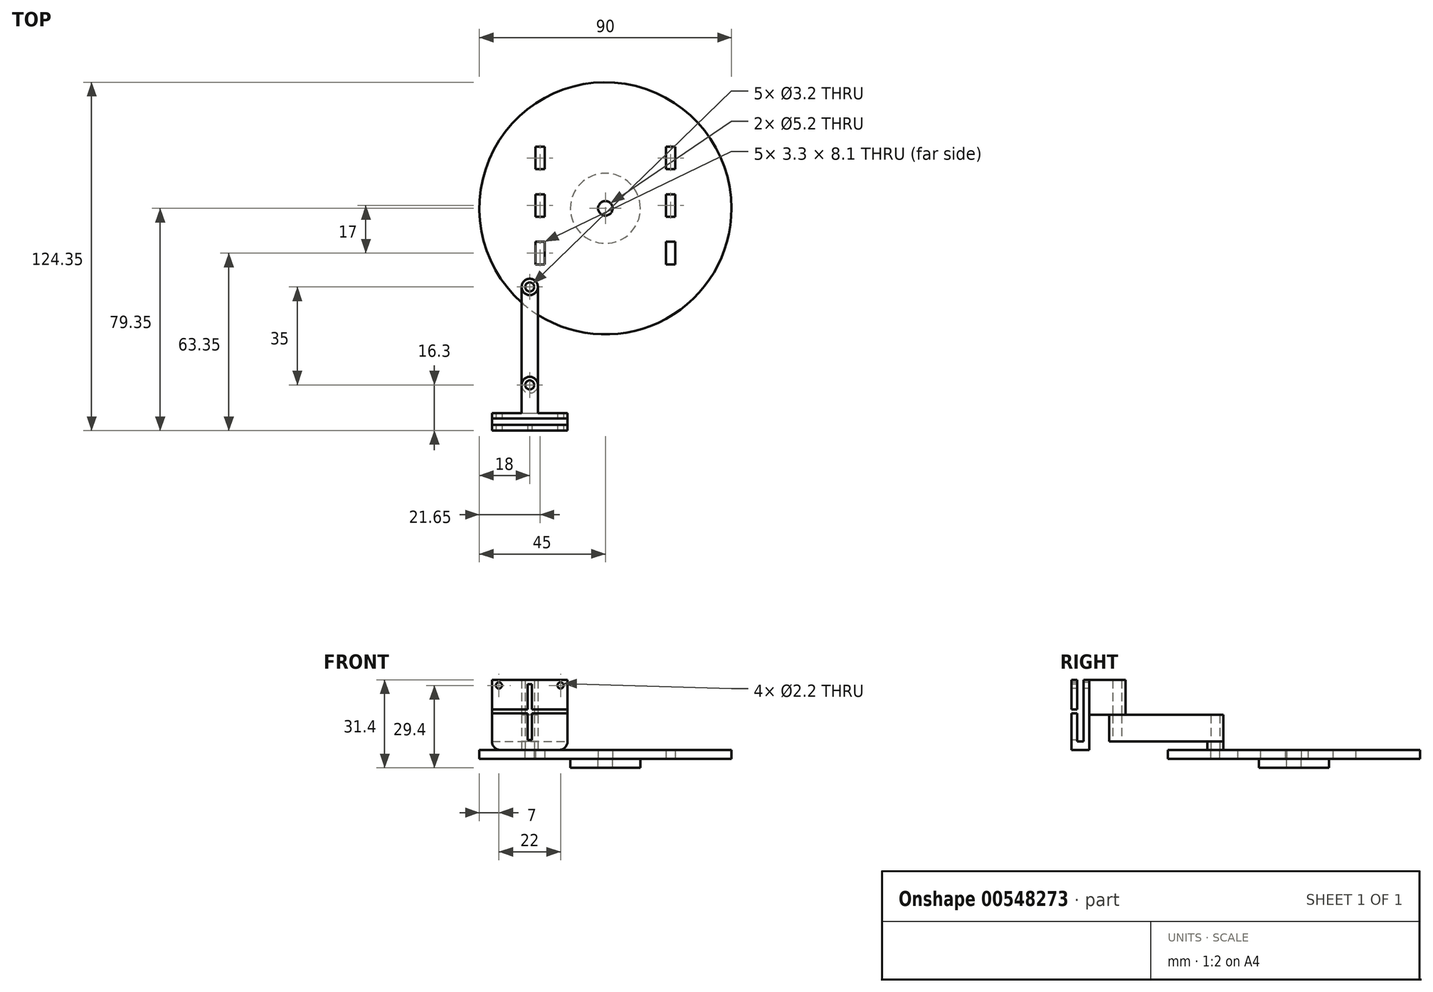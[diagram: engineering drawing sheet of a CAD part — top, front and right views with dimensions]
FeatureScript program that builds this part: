
annotation { "Feature Type Name" : "Feature", "Feature Type Description" : "" }
export const myFeature = defineFeature(function(context is Context, id is Id, definition is map)
    precondition{}
    {
        {
            var Q0;
            Q0=qCreatedBy(makeId("Top.planeOp"),FACE);
            var sketch = newSketch(context, id + "F0", { "sketchPlane" : qUnion([Q0])});
            skCircle(sketch, "E0", {"center": v(0, 0) * mm, "radius": 35.36 * mm});
            skLineSegment(sketch, "E1.bottom", {"start": v(25, 25) * mm, "end": v(-25, 25) * mm});
            skLineSegment(sketch, "E1.top", {"start": v(25, -25) * mm, "end": v(-25, -25) * mm});
            skLineSegment(sketch, "E1.left", {"start": v(25, 25) * mm, "end": v(25, -25) * mm});
            skLineSegment(sketch, "E1.right", {"start": v(-25, 25) * mm, "end": v(-25, -25) * mm});
            skLineSegment(sketch, "E2.bottom", {"start": v(-25, 22.05) * mm, "end": v(-21.7, 22.05) * mm});
            skLineSegment(sketch, "E2.top", {"start": v(-25, 13.95) * mm, "end": v(-21.7, 13.95) * mm});
            skLineSegment(sketch, "E2.left", {"start": v(-25, 22.05) * mm, "end": v(-25, 13.95) * mm});
            skLineSegment(sketch, "E2.right", {"start": v(-21.7, 22.05) * mm, "end": v(-21.7, 13.95) * mm});
            skLineSegment(sketch, "E3.bottom", {"start": v(-25, 5.05) * mm, "end": v(-21.7, 5.05) * mm});
            skLineSegment(sketch, "E3.top", {"start": v(-25, -3.05) * mm, "end": v(-21.7, -3.05) * mm});
            skLineSegment(sketch, "E3.left", {"start": v(-25, 5.05) * mm, "end": v(-25, -3.05) * mm});
            skLineSegment(sketch, "E3.right", {"start": v(-21.7, 5.05) * mm, "end": v(-21.7, -3.05) * mm});
            skLineSegment(sketch, "E4.bottom", {"start": v(-25, -11.95) * mm, "end": v(-21.7, -11.95) * mm});
            skLineSegment(sketch, "E4.top", {"start": v(-25, -20.05) * mm, "end": v(-21.7, -20.05) * mm});
            skLineSegment(sketch, "E4.left", {"start": v(-25, -11.95) * mm, "end": v(-25, -20.05) * mm});
            skLineSegment(sketch, "E4.right", {"start": v(-21.7, -11.95) * mm, "end": v(-21.7, -20.05) * mm});
            skLineSegment(sketch, "E5.bottom", {"start": v(25, 22.05) * mm, "end": v(21.7, 22.05) * mm});
            skLineSegment(sketch, "E5.top", {"start": v(25, 13.95) * mm, "end": v(21.7, 13.95) * mm});
            skLineSegment(sketch, "E5.left", {"start": v(25, 22.05) * mm, "end": v(25, 13.95) * mm});
            skLineSegment(sketch, "E5.right", {"start": v(21.7, 22.05) * mm, "end": v(21.7, 13.95) * mm});
            skLineSegment(sketch, "E6.bottom", {"start": v(25, 5.05) * mm, "end": v(21.7, 5.05) * mm});
            skLineSegment(sketch, "E6.top", {"start": v(25, -3.05) * mm, "end": v(21.7, -3.05) * mm});
            skLineSegment(sketch, "E6.left", {"start": v(25, 5.05) * mm, "end": v(25, -3.05) * mm});
            skLineSegment(sketch, "E6.right", {"start": v(21.7, 5.05) * mm, "end": v(21.7, -3.05) * mm});
            skLineSegment(sketch, "E7.bottom", {"start": v(25, -11.95) * mm, "end": v(21.6, -11.95) * mm});
            skLineSegment(sketch, "E7.top", {"start": v(25, -20.05) * mm, "end": v(21.6, -20.05) * mm});
            skLineSegment(sketch, "E7.left", {"start": v(25, -11.95) * mm, "end": v(25, -20.05) * mm});
            skLineSegment(sketch, "E7.right", {"start": v(21.6, -11.95) * mm, "end": v(21.6, -20.05) * mm});
            skCircle(sketch, "E8", {"center": v(0, 0) * mm, "radius": 2.6 * mm});
            skSolve(sketch);
        }
        {
            var Q0;
            Q0=qSketchRegion(id+"F0",true);
            extrude(context, id + "F1", {"entities" : qUnion([Q0]), "depth" : 3.2 * mm, "offsetDistance" : 25 * mm});
        }
        {
            var Q0;
            Q0=qCreatedBy(makeId("Top.planeOp"),FACE);
            var sketch = newSketch(context, id + "F2", { "sketchPlane" : qUnion([Q0])});
            skCircle(sketch, "E9", {"center": v(0, 0) * mm, "radius": 45 * mm});
            skCircle(sketch, "E10", {"center": v(0, 0) * mm, "radius": 35.36 * mm});
            skSolve(sketch);
        }
        {
            var Q0;
            Q0=qSketchRegion(id+"F2",true);
            var Q1;
            Q1=makeQuery(id+"F1.opExtrude","CAP_FACE",FACE,{"disambiguationData":[OSD([sQuery(id+"F0.wireOp",EDGE,"E0"),sQuery(id+"F0.wireOp",EDGE,"E2.bottom"),sQuery(id+"F0.wireOp",EDGE,"E2.top"),sQuery(id+"F0.wireOp",EDGE,"E2.left"),sQuery(id+"F0.wireOp",EDGE,"E2.right"),sQuery(id+"F0.wireOp",EDGE,"E3.bottom"),sQuery(id+"F0.wireOp",EDGE,"E3.top"),sQuery(id+"F0.wireOp",EDGE,"E3.left"),sQuery(id+"F0.wireOp",EDGE,"E3.right"),sQuery(id+"F0.wireOp",EDGE,"E4.bottom"),sQuery(id+"F0.wireOp",EDGE,"E4.top"),sQuery(id+"F0.wireOp",EDGE,"E4.left"),sQuery(id+"F0.wireOp",EDGE,"E4.right"),sQuery(id+"F0.wireOp",EDGE,"E5.bottom"),sQuery(id+"F0.wireOp",EDGE,"E5.top"),sQuery(id+"F0.wireOp",EDGE,"E5.left"),sQuery(id+"F0.wireOp",EDGE,"E5.right"),sQuery(id+"F0.wireOp",EDGE,"E6.bottom"),sQuery(id+"F0.wireOp",EDGE,"E6.top"),sQuery(id+"F0.wireOp",EDGE,"E6.left"),sQuery(id+"F0.wireOp",EDGE,"E6.right"),sQuery(id+"F0.wireOp",EDGE,"E7.bottom"),sQuery(id+"F0.wireOp",EDGE,"E7.top"),sQuery(id+"F0.wireOp",EDGE,"E7.left"),sQuery(id+"F0.wireOp",EDGE,"E7.right"),sQuery(id+"F0.wireOp",EDGE,"E8")])],"isStart":false});
            extrude(context, id + "F3", {"entities" : qUnion([Q0]), "operationType" : NewBodyOperationType.ADD, "endBound" : BoundingType.UP_TO_SURFACE, "depth" : 25 * mm, "endBoundEntityFace" : qUnion([Q1]), "offsetDistance" : 25 * mm});
        }
        {
            var Q0;
            {var subQ0=sQuery(id+"F0.wireOp",EDGE,"E8");var subQ1=sQuery(id+"F0.wireOp",EDGE,"E7.right");var subQ2=sQuery(id+"F0.wireOp",EDGE,"E7.left");var subQ3=sQuery(id+"F0.wireOp",EDGE,"E7.top");var subQ4=sQuery(id+"F0.wireOp",EDGE,"E7.bottom");var subQ5=sQuery(id+"F0.wireOp",EDGE,"E6.right");var subQ6=sQuery(id+"F0.wireOp",EDGE,"E6.left");var subQ7=sQuery(id+"F0.wireOp",EDGE,"E6.top");var subQ8=sQuery(id+"F0.wireOp",EDGE,"E6.bottom");var subQ9=sQuery(id+"F0.wireOp",EDGE,"E5.right");var subQ10=sQuery(id+"F0.wireOp",EDGE,"E5.left");var subQ11=sQuery(id+"F0.wireOp",EDGE,"E5.top");var subQ12=sQuery(id+"F0.wireOp",EDGE,"E5.bottom");var subQ13=sQuery(id+"F0.wireOp",EDGE,"E4.right");var subQ14=sQuery(id+"F0.wireOp",EDGE,"E4.left");var subQ15=sQuery(id+"F0.wireOp",EDGE,"E4.top");var subQ16=sQuery(id+"F0.wireOp",EDGE,"E4.bottom");var subQ17=sQuery(id+"F0.wireOp",EDGE,"E3.right");var subQ18=sQuery(id+"F0.wireOp",EDGE,"E3.left");var subQ19=sQuery(id+"F0.wireOp",EDGE,"E3.top");var subQ20=sQuery(id+"F0.wireOp",EDGE,"E3.bottom");var subQ21=sQuery(id+"F0.wireOp",EDGE,"E2.right");var subQ22=sQuery(id+"F0.wireOp",EDGE,"E2.left");var subQ23=sQuery(id+"F0.wireOp",EDGE,"E2.top");var subQ24=sQuery(id+"F0.wireOp",EDGE,"E2.bottom");var subQ25=sQuery(id+"F0.wireOp",EDGE,"E0");Q0=makeQuery(id+"F3.boolean.opBoolean","MERGE",FACE,{"derivedFrom":[makeQuery(id+"F1.opExtrude","CAP_FACE",FACE,{"disambiguationData":[OSD([subQ25,subQ24,subQ23,subQ22,subQ21,subQ20,subQ19,subQ18,subQ17,subQ16,subQ15,subQ14,subQ13,subQ12,subQ11,subQ10,subQ9,subQ8,subQ7,subQ6,subQ5,subQ4,subQ3,subQ2,subQ1,subQ0])],"isStart":false}),makeQuery(id+"F3.opExtrude","CAP_FACE",FACE,{"disambiguationData":[OSD([subQ25,subQ24,subQ23,subQ22,subQ21,subQ20,subQ19,subQ18,subQ17,subQ16,subQ15,subQ14,subQ13,subQ12,subQ11,subQ10,subQ9,subQ8,subQ7,subQ6,subQ5,subQ4,subQ3,subQ2,subQ1,subQ0])],"isStart":false})]});}
            var sketch = newSketch(context, id + "F4", { "sketchPlane" : qUnion([Q0])});
            skCircle(sketch, "E11", {"center": v(-27, -28.05) * mm, "radius": 1.6 * mm});
            skCircle(sketch, "E12", {"center": v(-27, -28.05) * mm, "radius": 2.9 * mm});
            skSolve(sketch);
        }
        {
            var Q0;
            Q0=makeQuery(id+"F4.imprint","IMPRINT",FACE,{"disambiguationData":[TD([[makeQuery(id+"F4.imprint","IMPRINT",EDGE,{"derivedFrom":sQuery(id+"F4.wireOp",EDGE,"E11")}),1.0]])]});
            var Q1;
            Q1=sQuery(id+"F4.wireOp",EDGE,"E11");
            var Q2;
            Q2=makeQuery(id+"F3.boolean.opBoolean","MERGE",FACE,{"derivedFrom":[makeQuery(id+"F1.opExtrude","CAP_FACE",FACE,{"disambiguationData":[OSD([sQuery(id+"F0.wireOp",EDGE,"E0"),sQuery(id+"F0.wireOp",EDGE,"E2.bottom"),sQuery(id+"F0.wireOp",EDGE,"E2.top"),sQuery(id+"F0.wireOp",EDGE,"E2.left"),sQuery(id+"F0.wireOp",EDGE,"E2.right"),sQuery(id+"F0.wireOp",EDGE,"E3.bottom"),sQuery(id+"F0.wireOp",EDGE,"E3.top"),sQuery(id+"F0.wireOp",EDGE,"E3.left"),sQuery(id+"F0.wireOp",EDGE,"E3.right"),sQuery(id+"F0.wireOp",EDGE,"E4.bottom"),sQuery(id+"F0.wireOp",EDGE,"E4.top"),sQuery(id+"F0.wireOp",EDGE,"E4.left"),sQuery(id+"F0.wireOp",EDGE,"E4.right"),sQuery(id+"F0.wireOp",EDGE,"E5.bottom"),sQuery(id+"F0.wireOp",EDGE,"E5.top"),sQuery(id+"F0.wireOp",EDGE,"E5.left"),sQuery(id+"F0.wireOp",EDGE,"E5.right"),sQuery(id+"F0.wireOp",EDGE,"E6.bottom"),sQuery(id+"F0.wireOp",EDGE,"E6.top"),sQuery(id+"F0.wireOp",EDGE,"E6.left"),sQuery(id+"F0.wireOp",EDGE,"E6.right"),sQuery(id+"F0.wireOp",EDGE,"E7.bottom"),sQuery(id+"F0.wireOp",EDGE,"E7.top"),sQuery(id+"F0.wireOp",EDGE,"E7.left"),sQuery(id+"F0.wireOp",EDGE,"E7.right"),sQuery(id+"F0.wireOp",EDGE,"E8")])],"isStart":true}),makeQuery(id+"F3.opExtrude","CAP_FACE",FACE,{"disambiguationData":[OSD([sQuery(id+"F2.wireOp",EDGE,"E9"),sQuery(id+"F2.wireOp",EDGE,"E10")])],"isStart":true})]});
            extrude(context, id + "F5", {"entities" : qUnion([Q0]), "operationType" : NewBodyOperationType.REMOVE, "surfaceEntities" : qUnion([Q1]), "endBound" : BoundingType.UP_TO_SURFACE, "oppositeDirection" : true, "depth" : 25 * mm, "endBoundEntityFace" : qUnion([Q2]), "offsetDistance" : 25 * mm});
        }
        {
            var Q0;
            Q0=makeQuery(id+"F4.imprint","IMPRINT",FACE,{"disambiguationData":[TD([[makeQuery(id+"F4.imprint","IMPRINT",EDGE,{"derivedFrom":sQuery(id+"F4.wireOp",EDGE,"E11")}),-1.0]])]});
            extrude(context, id + "F6", {"entities" : qUnion([Q0]), "depth" : 2.5 * mm, "offsetDistance" : 25 * mm});
        }
        {
            var Q0;
            Q0=makeQuery(id+"F4.imprint","IMPRINT",FACE,{"disambiguationData":[TD([[makeQuery(id+"F4.imprint","IMPRINT",EDGE,{"derivedFrom":sQuery(id+"F4.wireOp",EDGE,"IzYP4Wh4-Jip2-t4EX-ThSt-IXmmCnc5qann")}),-1.0]])]});
            var Q1;
            {var subQ0=sQuery(id+"F4.wireOp",EDGE,"7peC47Pw-5aqN-fUO1-vEJ7-lQEhbhiZa9DA");var subQ1=sQuery(id+"F4.wireOp",EDGE,"wxSrbtV1-SH39-PG1R-bbc8-Dl0xVSDKGow7");var subQ2=makeQuery(id+"F4.imprint","INTERSECT",VERTEX,{"derivedFrom":[subQ1,subQ0]});Q1=makeQuery(id+"F4.imprint","IMPRINT",FACE,{"disambiguationData":[TD([[makeQuery(id+"F4.imprint","IMPRINT",EDGE,{"disambiguationData":[TD([[subQ2,1.0]])],"derivedFrom":subQ0}),-1.0]])]});}
            var Q2;
            Q2=makeQuery(id+"F4.imprint","IMPRINT",FACE,{"disambiguationData":[TD([[makeQuery(id+"F4.imprint","IMPRINT",EDGE,{"derivedFrom":sQuery(id+"F4.wireOp",EDGE,"E11")}),-1.0]])]});
            var Q3;
            {var subQ0=sQuery(id+"F4.wireOp",EDGE,"wxSrbtV1-SH39-PG1R-bbc8-Dl0xVSDKGow7");var subQ1=sQuery(id+"F4.wireOp",EDGE,"E12");var subQ2=makeQuery(id+"F4.imprint","INTERSECT",VERTEX,{"derivedFrom":[subQ1,subQ0]});Q3=makeQuery(id+"F4.imprint","IMPRINT",FACE,{"disambiguationData":[TD([[makeQuery(id+"F4.imprint","IMPRINT",EDGE,{"disambiguationData":[TD([[subQ2,-1.0]])],"derivedFrom":subQ1}),-1.0]])]});}
            var Q4;
            Q4=sQuery(id+"F4.wireOp",EDGE,"IzYP4Wh4-Jip2-t4EX-ThSt-IXmmCnc5qann");
            var Q5;
            Q5=sQuery(id+"F4.wireOp",EDGE,"7peC47Pw-5aqN-fUO1-vEJ7-lQEhbhiZa9DA");
            var Q6;
            Q6=sQuery(id+"F4.wireOp",EDGE,"9hU6XA7T-7hqy-5dnO-gkdG-iSiWrYzMhXLp");
            var Q7;
            Q7=sQuery(id+"F4.wireOp",EDGE,"wxSrbtV1-SH39-PG1R-bbc8-Dl0xVSDKGow7");
            var Q8;
            Q8=sQuery(id+"F4.wireOp",EDGE,"E11");
            var Q9;
            Q9=sQuery(id+"F4.wireOp",EDGE,"E12");
            extrude(context, id + "F7", {"entities" : qUnion([Q0, Q1, Q2, Q3]), "surfaceEntities" : qUnion([Q4, Q5, Q6, Q7, Q8, Q9]), "depth" : 12 * mm, "offsetDistance" : 25 * mm});
        }
        {
            var Q0;
            Q0=makeQuery(id+"F7.opExtrude","SWEPT_BODY",BODY,{"disambiguationData":[OSD([sQuery(id+"F4.wireOp",EDGE,"E11"),sQuery(id+"F4.wireOp",EDGE,"E12"),sQuery(id+"F4.wireOp",EDGE,"wxSrbtV1-SH39-PG1R-bbc8-Dl0xVSDKGow7"),sQuery(id+"F4.wireOp",EDGE,"9hU6XA7T-7hqy-5dnO-gkdG-iSiWrYzMhXLp"),sQuery(id+"F4.wireOp",EDGE,"7peC47Pw-5aqN-fUO1-vEJ7-lQEhbhiZa9DA"),sQuery(id+"F4.wireOp",EDGE,"IzYP4Wh4-Jip2-t4EX-ThSt-IXmmCnc5qann")])]});
            var Q1;
            Q1=makeQuery(id+"F6.opExtrude","SWEPT_BODY",BODY,{"disambiguationData":[OSD([sQuery(id+"F4.wireOp",EDGE,"E11"),sQuery(id+"F4.wireOp",EDGE,"E12")])]});
            deleteBodies(context, id + "F8", {"entities" : qUnion([Q0, Q1])});
        }
        {
            var Q0;
            Q0=makeQuery(id+"F4.imprint","IMPRINT",FACE,{"disambiguationData":[TD([[makeQuery(id+"F4.imprint","IMPRINT",EDGE,{"derivedFrom":sQuery(id+"F4.wireOp",EDGE,"E11")}),-1.0]])]});
            extrude(context, id + "F9", {"entities" : qUnion([Q0]), "depth" : 3 * mm, "offsetDistance" : 25 * mm});
        }
        {
            var Q0;
            Q0=makeQuery(id+"F9.opExtrude","CAP_FACE",FACE,{"disambiguationData":[OSD([sQuery(id+"F4.wireOp",EDGE,"E11"),sQuery(id+"F4.wireOp",EDGE,"E12")])],"isStart":false});
            var sketch = newSketch(context, id + "F10", { "sketchPlane" : qUnion([Q0])});
            skCircle(sketch, "E13", {"center": v(-27, -28.05) * mm, "radius": 1.6 * mm});
            skCircle(sketch, "E14", {"center": v(-27, -28.05) * mm, "radius": 2.9 * mm});
            skCircle(sketch, "E15", {"center": v(-27, -63.05) * mm, "radius": 1.6 * mm});
            skCircle(sketch, "E16", {"center": v(-27, -63.05) * mm, "radius": 2.9 * mm});
            skLineSegment(sketch, "E17", {"start": v(-29.9, -28.05) * mm, "end": v(-29.9, -63.05) * mm});
            skLineSegment(sketch, "E18", {"start": v(-24.1, -28.05) * mm, "end": v(-24.1, -63.05) * mm});
            skSolve(sketch);
        }
        {
            var Q0;
            Q0=qSketchRegion(id+"F10",true);
            extrude(context, id + "F11", {"entities" : qUnion([Q0]), "depth" : 9.5 * mm, "offsetDistance" : 25 * mm});
        }
        {
            var Q0;
            Q0=makeQuery(id+"F3.boolean.opBoolean","MERGE",FACE,{"derivedFrom":[makeQuery(id+"F1.opExtrude","CAP_FACE",FACE,{"disambiguationData":[OSD([sQuery(id+"F0.wireOp",EDGE,"E0"),sQuery(id+"F0.wireOp",EDGE,"E2.bottom"),sQuery(id+"F0.wireOp",EDGE,"E2.top"),sQuery(id+"F0.wireOp",EDGE,"E2.left"),sQuery(id+"F0.wireOp",EDGE,"E2.right"),sQuery(id+"F0.wireOp",EDGE,"E3.bottom"),sQuery(id+"F0.wireOp",EDGE,"E3.top"),sQuery(id+"F0.wireOp",EDGE,"E3.left"),sQuery(id+"F0.wireOp",EDGE,"E3.right"),sQuery(id+"F0.wireOp",EDGE,"E4.bottom"),sQuery(id+"F0.wireOp",EDGE,"E4.top"),sQuery(id+"F0.wireOp",EDGE,"E4.left"),sQuery(id+"F0.wireOp",EDGE,"E4.right"),sQuery(id+"F0.wireOp",EDGE,"E5.bottom"),sQuery(id+"F0.wireOp",EDGE,"E5.top"),sQuery(id+"F0.wireOp",EDGE,"E5.left"),sQuery(id+"F0.wireOp",EDGE,"E5.right"),sQuery(id+"F0.wireOp",EDGE,"E6.bottom"),sQuery(id+"F0.wireOp",EDGE,"E6.top"),sQuery(id+"F0.wireOp",EDGE,"E6.left"),sQuery(id+"F0.wireOp",EDGE,"E6.right"),sQuery(id+"F0.wireOp",EDGE,"E7.bottom"),sQuery(id+"F0.wireOp",EDGE,"E7.top"),sQuery(id+"F0.wireOp",EDGE,"E7.left"),sQuery(id+"F0.wireOp",EDGE,"E7.right"),sQuery(id+"F0.wireOp",EDGE,"E8")])],"isStart":true}),makeQuery(id+"F3.opExtrude","CAP_FACE",FACE,{"disambiguationData":[OSD([sQuery(id+"F2.wireOp",EDGE,"E9"),sQuery(id+"F2.wireOp",EDGE,"E10")])],"isStart":true})]});
            var sketch = newSketch(context, id + "F12", { "sketchPlane" : qUnion([Q0])});
            skCircle(sketch, "E19", {"center": v(0, 0) * mm, "radius": 12.5 * mm});
            skSolve(sketch);
        }
        {
            var Q0;
            Q0=makeQuery(id+"F12.imprint","IMPRINT",FACE,{"disambiguationData":[TD([[makeQuery(id+"F12.imprint","IMPRINT",EDGE,{"derivedFrom":sQuery(id+"F12.wireOp",EDGE,"E19")}),1.0]])]});
            extrude(context, id + "F13", {"entities" : qUnion([Q0]), "depth" : 3.2 * mm, "offsetDistance" : 25 * mm});
        }
        {
            var Q0;
            Q0=makeQuery(id+"F11.opExtrude","CAP_FACE",FACE,{"disambiguationData":[OSD([sQuery(id+"F10.wireOp",EDGE,"E13"),sQuery(id+"F10.wireOp",EDGE,"E14"),sQuery(id+"F10.wireOp",EDGE,"E15"),sQuery(id+"F10.wireOp",EDGE,"E16"),sQuery(id+"F10.wireOp",EDGE,"E17"),sQuery(id+"F10.wireOp",EDGE,"E18")])],"isStart":false});
            var sketch = newSketch(context, id + "F14", { "sketchPlane" : qUnion([Q0])});
            skCircle(sketch, "E20", {"center": v(-27, -63.05) * mm, "radius": 1.6 * mm});
            skCircle(sketch, "E21", {"center": v(-27, -63.05) * mm, "radius": 2.9 * mm});
            skLineSegment(sketch, "E22", {"start": v(-29.9, -63.05) * mm, "end": v(-29.9, -73.05) * mm});
            skLineSegment(sketch, "E23", {"start": v(-24.1, -63.05) * mm, "end": v(-24.1, -73.05) * mm});
            skLineSegment(sketch, "E24", {"start": v(-29.9, -73.05) * mm, "end": v(-24.1, -73.05) * mm});
            skSolve(sketch);
        }
        {
            var Q0;
            Q0=qSketchRegion(id+"F14",true);
            extrude(context, id + "F15", {"entities" : qUnion([Q0]), "depth" : 12.5 * mm, "offsetDistance" : 25 * mm});
        }
        {
            var Q0;
            Q0=makeQuery(id+"F15.opExtrude","CAP_FACE",FACE,{"disambiguationData":[OSD([sQuery(id+"F14.wireOp",EDGE,"E20"),sQuery(id+"F14.wireOp",EDGE,"E21"),sQuery(id+"F14.wireOp",EDGE,"E22"),sQuery(id+"F14.wireOp",EDGE,"E23"),sQuery(id+"F14.wireOp",EDGE,"E24")])],"isStart":false});
            var sketch = newSketch(context, id + "F16", { "sketchPlane" : qUnion([Q0])});
            skLineSegment(sketch, "E25", {"start": v(-40.5, -73.05) * mm, "end": v(-13.5, -73.05) * mm});
            skLineSegment(sketch, "E26", {"start": v(-40.5, -73.05) * mm, "end": v(-40.5, -79.35) * mm});
            skLineSegment(sketch, "E27", {"start": v(-13.5, -73.05) * mm, "end": v(-13.5, -79.35) * mm});
            skLineSegment(sketch, "E28", {"start": v(-40.5, -79.35) * mm, "end": v(-13.5, -79.35) * mm});
            skLineSegment(sketch, "E29", {"start": v(-40.5, -75.05) * mm, "end": v(-13.5, -75.05) * mm});
            skLineSegment(sketch, "E30", {"start": v(-40.5, -77.35) * mm, "end": v(-13.5, -77.35) * mm});
            skLineSegment(sketch, "E31", {"start": v(-27.75, -77.35) * mm, "end": v(-27.75, -79.35) * mm});
            skLineSegment(sketch, "E32", {"start": v(-26.25, -77.35) * mm, "end": v(-26.25, -79.35) * mm});
            skSolve(sketch);
        }
        {
            var Q0;
            Q0=qSketchRegion(id+"F16",true);
            extrude(context, id + "F17", {"entities" : qUnion([Q0]), "operationType" : NewBodyOperationType.ADD, "oppositeDirection" : true, "depth" : 25 * mm, "offsetDistance" : 25 * mm});
        }
        {
            var Q0;
            Q0=makeQuery(id+"F17.opExtrude","CAP_EDGE",EDGE,{"disambiguationData":[OSD([sQuery(id+"F16.wireOp",EDGE,"E26")])],"isStart":false});
            var Q1;
            Q1=makeQuery(id+"F17.opExtrude","CAP_EDGE",EDGE,{"disambiguationData":[OSD([sQuery(id+"F16.wireOp",EDGE,"E27")])],"isStart":false});
            fillet(context, id + "F18", {"entities" : qUnion([Q0, Q1]), "radius" : 3 * mm, "tangentPropagation" : true, "allowEdgeOverflow" : false});
        }
        {
            var Q0;
            {var subQ0=sQuery(id+"F16.wireOp",EDGE,"E29");Q0=makeQuery(id+"F16.imprint","IMPRINT",FACE,{"disambiguationData":[TD([[makeQuery(id+"F16.imprint","IMPRINT",EDGE,{"derivedFrom":subQ0}),-1.0]])]});}
            extrude(context, id + "F19", {"entities" : qUnion([Q0]), "operationType" : NewBodyOperationType.REMOVE, "oppositeDirection" : true, "depth" : 22 * mm, "offsetDistance" : 25 * mm});
        }
        {
            var Q0;
            {var subQ0=sQuery(id+"F16.wireOp",EDGE,"E28");Q0=makeQuery(id+"F16.imprint","IMPRINT",FACE,{"disambiguationData":[TD([[makeQuery(id+"F16.imprint","IMPRINT",EDGE,{"derivedFrom":subQ0}),1.0]])]});}
            extrude(context, id + "F20", {"entities" : qUnion([Q0]), "operationType" : NewBodyOperationType.REMOVE, "oppositeDirection" : true, "depth" : 12 * mm, "offsetDistance" : 25 * mm});
        }
        {
            var Q0;
            {var subQ0=sQuery(id+"F16.wireOp",EDGE,"E31");Q0=makeQuery(id+"F16.imprint","IMPRINT",FACE,{"disambiguationData":[TD([[makeQuery(id+"F16.imprint","IMPRINT",EDGE,{"derivedFrom":subQ0}),1.0]])]});}
            extrude(context, id + "F21", {"entities" : qUnion([Q0]), "operationType" : NewBodyOperationType.REMOVE, "oppositeDirection" : true, "depth" : 21.5 * mm, "offsetDistance" : 25 * mm});
        }
        {
            var Q0;
            Q0=makeQuery(id+"F17.opExtrude","SWEPT_FACE",FACE,{"disambiguationData":[OSD([sQuery(id+"F16.wireOp",EDGE,"E28")])]});
            var sketch = newSketch(context, id + "F22", { "sketchPlane" : qUnion([Q0])});
            skLineSegment(sketch, "E33", {"start": v(-27.75, 17.7) * mm, "end": v(-40.5, 17.7) * mm});
            skLineSegment(sketch, "E34", {"start": v(-26.25, 17.7) * mm, "end": v(-13.5, 17.7) * mm});
            skLineSegment(sketch, "E35", {"start": v(-13.5, 17.7) * mm, "end": v(-13.5, 28.2) * mm});
            skLineSegment(sketch, "E36", {"start": v(-40.5, 17.7) * mm, "end": v(-40.5, 28.2) * mm});
            skLineSegment(sketch, "E37", {"start": v(-40.5, 28.2) * mm, "end": v(-13.5, 28.2) * mm});
            skLineSegment(sketch, "E38", {"start": v(-27.75, 17.7) * mm, "end": v(-27.75, 26.7) * mm});
            skLineSegment(sketch, "E39", {"start": v(-26.25, 17.7) * mm, "end": v(-26.25, 26.7) * mm});
            skLineSegment(sketch, "E40", {"start": v(-27.75, 26.7) * mm, "end": v(-26.25, 26.7) * mm});
            skCircle(sketch, "E41", {"center": v(-38, 26.2) * mm, "radius": 1.1 * mm});
            skCircle(sketch, "E42", {"center": v(-16, 26.2) * mm, "radius": 1.1 * mm});
            skSolve(sketch);
        }
        {
            var Q0;
            Q0=qSketchRegion(id+"F22",true);
            var Q1;
            {var subQ0=sQuery(id+"F16.wireOp",EDGE,"E30");var subQ2=sQuery(id+"F16.wireOp",EDGE,"E26");Q1=makeQuery(id+"F21.boolean.opBoolean","SPLIT",FACE,{"disambiguationData":[TD([makeQuery(id+"F17.opExtrude","SWEPT_FACE",FACE,{"disambiguationData":[OSD([subQ2])]})])],"derivedFrom":makeQuery(id+"F19.boolean.opBoolean","COPY",FACE,{"derivedFrom":makeQuery(id+"F19.opExtrude","SWEPT_FACE",FACE,{"disambiguationData":[OSD([subQ0])]})})});}
            extrude(context, id + "F23", {"entities" : qUnion([Q0]), "endBound" : BoundingType.UP_TO_SURFACE, "oppositeDirection" : true, "depth" : 25 * mm, "endBoundEntityFace" : qUnion([Q1]), "offsetDistance" : 25 * mm});
        }
        {
            var Q0;
            Q0=makeQuery(id+"F19.boolean.opBoolean","COPY",FACE,{"derivedFrom":makeQuery(id+"F19.opExtrude","SWEPT_FACE",FACE,{"disambiguationData":[OSD([sQuery(id+"F16.wireOp",EDGE,"E29")])]})});
            var sketch = newSketch(context, id + "F24", { "sketchPlane" : qUnion([Q0])});
            skCircle(sketch, "E43", {"center": v(-38, 26.2) * mm, "radius": 1.1 * mm});
            skCircle(sketch, "E44", {"center": v(-16, 26.2) * mm, "radius": 1.1 * mm});
            skSolve(sketch);
        }
        {
            var Q0;
            Q0=qSketchRegion(id+"F24",true);
            var Q1;
            Q1=makeQuery(id+"F17.opExtrude","SWEPT_FACE",FACE,{"disambiguationData":[OSD([sQuery(id+"F16.wireOp",EDGE,"E25")])]});
            extrude(context, id + "F25", {"entities" : qUnion([Q0]), "operationType" : NewBodyOperationType.REMOVE, "endBound" : BoundingType.UP_TO_SURFACE, "oppositeDirection" : true, "depth" : 25 * mm, "endBoundEntityFace" : qUnion([Q1]), "offsetDistance" : 25 * mm});
        }
    });
